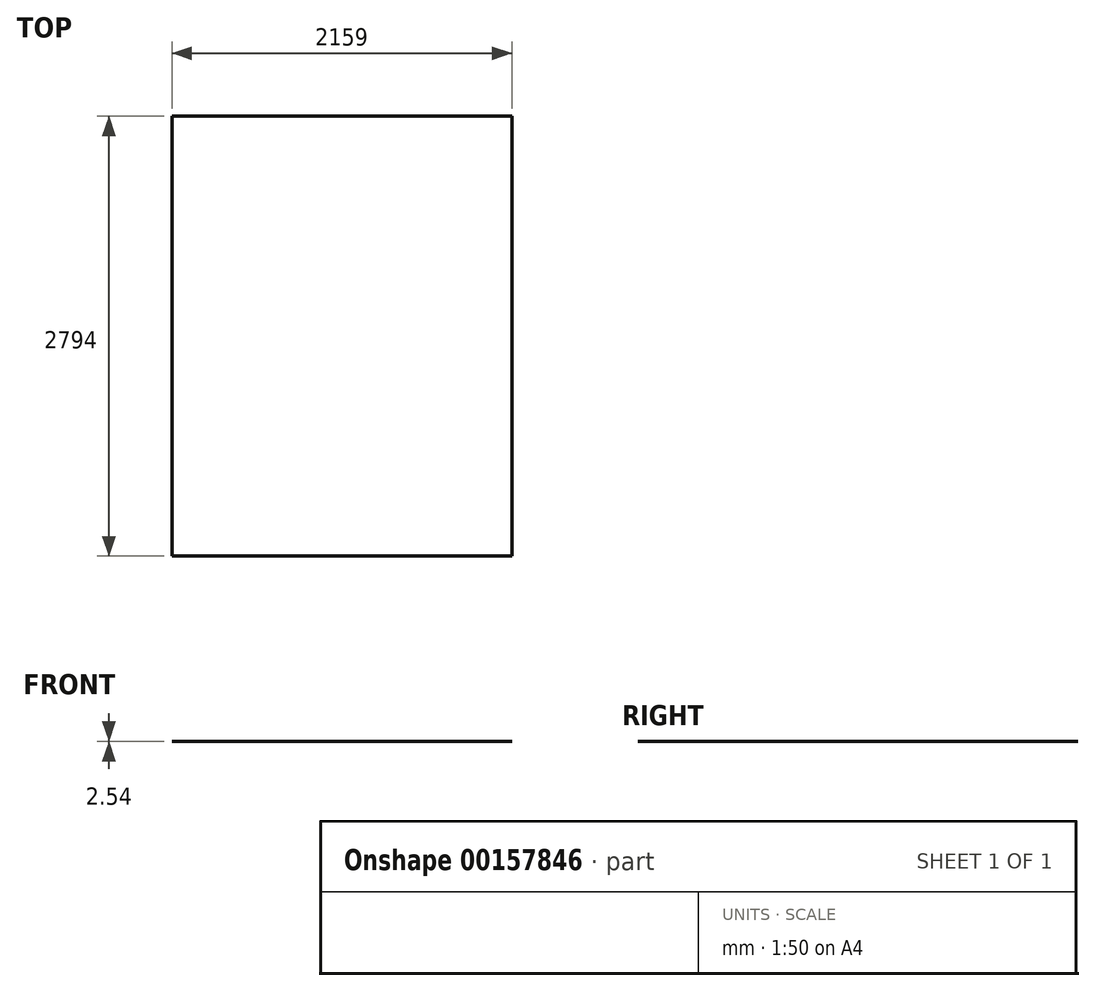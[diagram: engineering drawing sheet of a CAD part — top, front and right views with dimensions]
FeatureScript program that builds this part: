
annotation { "Feature Type Name" : "Feature", "Feature Type Description" : "" }
export const myFeature = defineFeature(function(context is Context, id is Id, definition is map)
    precondition{}
    {
        {
            var Q0;
            Q0=qCreatedBy(makeId("Top.planeOp"),FACE);
            var sketch = newSketch(context, id + "F0", { "sketchPlane" : qUnion([Q0])});
            skLineSegment(sketch, "E0.bottom", {"start": v(0, 0) * mm, "end": v(2159, 0) * mm});
            skLineSegment(sketch, "E0.top", {"start": v(0, 2794) * mm, "end": v(2159, 2794) * mm});
            skLineSegment(sketch, "E0.left", {"start": v(0, 0) * mm, "end": v(0, 2794) * mm});
            skLineSegment(sketch, "E0.right", {"start": v(2159, 0) * mm, "end": v(2159, 2794) * mm});
            skSolve(sketch);
        }
        {
            var Q0;
            Q0 = qSketchRegion(id + "F0", true);
            extrude(context, id + "F1", {"entities" : qUnion([Q0]), "depth" : 2.54 * mm});
        }
    });
